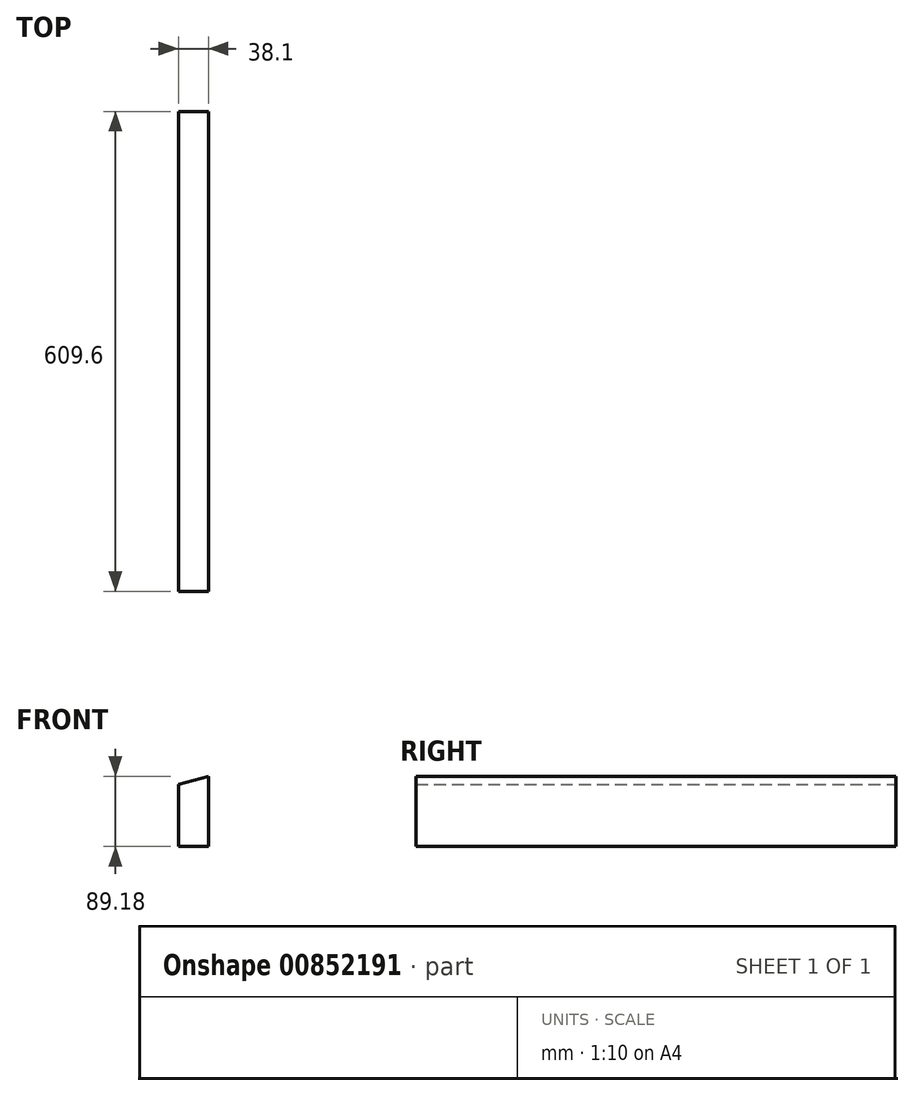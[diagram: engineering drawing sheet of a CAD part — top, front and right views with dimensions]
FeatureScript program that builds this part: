
annotation { "Feature Type Name" : "Feature", "Feature Type Description" : "" }
export const myFeature = defineFeature(function(context is Context, id is Id, definition is map)
    precondition{}
    {
        {
            var Q0;
            Q0=qCreatedBy(makeId("Front.planeOp"),FACE);
            var sketch = newSketch(context, id + "F0", { "sketchPlane" : qUnion([Q0])});
            skLineSegment(sketch, "E0", {"start": v(19.05, -44.45) * mm, "end": v(19.05, 44.45) * mm});
            skLineSegment(sketch, "E1", {"start": v(19.05, 44.45) * mm, "end": v(-19.05, 34.24) * mm});
            skLineSegment(sketch, "E2", {"start": v(-19.05, 34.24) * mm, "end": v(-19.05, -44.73) * mm});
            skLineSegment(sketch, "E3", {"start": v(-19.05, -44.73) * mm, "end": v(19.05, -44.45) * mm});
            skSolve(sketch);
        }
        {
            var Q0;
            Q0=qSketchRegion(id+"F0",true);
            extrude(context, id + "F1", {"entities" : qUnion([Q0]), "depth" : 609.6 * mm, "offsetDistance" : 25.4 * mm});
        }
    });
